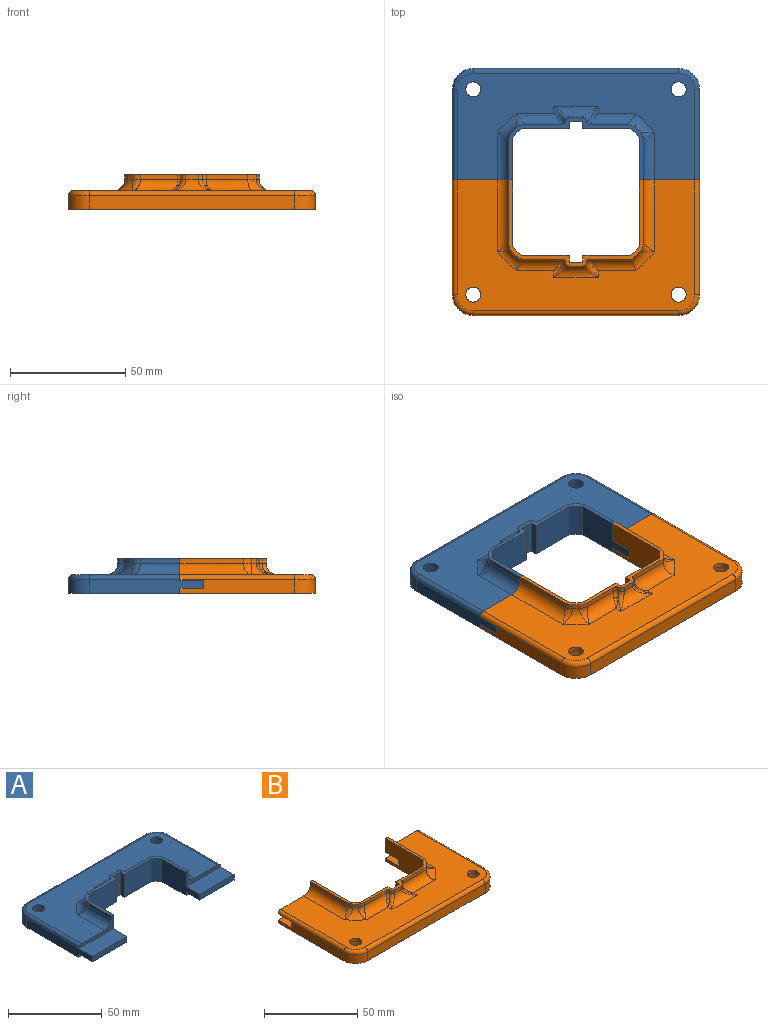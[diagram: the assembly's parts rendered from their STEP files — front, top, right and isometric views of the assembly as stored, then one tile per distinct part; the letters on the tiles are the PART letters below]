
ASSEMBLY  parts=2 mates=1
PART A: 73 faces, bbox 108.5x59.2x16.6 mm
  f0: plane 49.43x6mm, normal (1,0,0), area 272.4mm2, adj f1,f66,f67,f68,f69,f70,f71,f72
  f1: plane 26x10.2mm, normal (0,0,-1), area 265.2mm2, adj f0,f2,f66,f72
  f2: plane 28.6x15mm, normal (-1,0,0), area 313mm2, adj f1,f3,f65,f66,f67,f68,f71,f72
  f3: cylinder r=36.25mm len=15mm, axis (0,0,-1), area 82.4mm2, adj f2,f4,f65,f71
  f4: plane 20.62x15mm, normal (0,-1,0), area 309.3mm2, adj f3,f5,f65,f71
  f5: plane 15x3mm, normal (-1,0,0), area 45mm2, adj f4,f6,f65,f71
  f6: plane 15x6mm, normal (0,-1,0), area 90mm2, adj f5,f7,f65,f71
  f7: plane 15x3mm, normal (1,0,0), area 45mm2, adj f6,f8,f65,f71
  f8: plane 20.62x15mm, normal (0,-1,0), area 309.3mm2, adj f7,f9,f65,f71
  f9: cylinder r=36.25mm len=15mm, axis (0,0,-1), area 82.4mm2, adj f8,f10,f65,f71
  f10: plane 28.6x15mm, normal (1,0,0), area 313mm2, adj f9,f11,f61,f62,f63,f64,f65,f71
  f11: plane 26x10.2mm, normal (0,0,-1), area 265.2mm2, adj f10,f12,f61,f64
  f12: plane 49.43x6mm, normal (-1,0,0), area 272.4mm2, adj f11,f13,f60,f61,f62,f63,f64,f71
  f13: cylinder r=9.05mm len=9.05mm, axis (0,0,-1), area 85.3mm2, adj f12,f14,f59,f71
  f14: plane 88.9x6mm, normal (0,1,0), area 533.4mm2, adj f13,f15,f70,f71
  f15: cylinder r=2mm len=88.9mm, axis (1,0,0), area 279.3mm2, adj f14,f16,f17,f59
  f16: torus R=7.05mm, axis (0,0,1), area 41.1mm2, adj f15,f17,f69,f70
  f17: plane 103x46.28mm, normal (0,0,1), area 2712.4mm2, adj f15,f16,f18,f44,f45,f47,f48,f49
  f18: cylinder r=5mm len=20.73mm, axis (0,1,0), area 148.6mm2, adj f17,f19,f43,f68
  f19: bspline ~6.34x5.9mm, area 11.8mm2, adj f18,f20,f44
  f20: cylinder r=5mm len=3.4mm, axis (0,0,-1), area 7.5mm2, adj f19,f21,f43,f65
  f21: cylinder r=37.85mm len=2.04mm, axis (0,0,-1), area 5.8mm2, adj f20,f22,f44,f65
  f22: cylinder r=5mm len=3.4mm, axis (0,0,-1), area 7.5mm2, adj f21,f23,f42,f65
  f23: plane 16.26x2mm, normal (0,1,0), area 32.5mm2, adj f22,f24,f45,f65
  f24: cylinder r=1.5mm len=2mm, axis (0,0,-1), area 4.3mm2, adj f23,f25,f28,f65
  f25: bspline ~4.79x2.55mm, area 6.2mm2, adj f24,f26,f27,f45
  f26: bspline ~2.94x2.94mm, area 2.5mm2, adj f25,f45,f47
  f27: bspline ~7x7mm, area 13.9mm2, adj f25,f28,f47,f48
  f28: cylinder r=2mm len=2mm, axis (0,0,-1), area 5.7mm2, adj f24,f27,f29,f65
  f29: plane 5.2x2mm, normal (0,1,0), area 10.4mm2, adj f28,f30,f48,f65
  f30: cylinder r=2mm len=2mm, axis (0,0,-1), area 5.7mm2, adj f29,f31,f41,f65
  f31: cylinder r=1.5mm len=2mm, axis (0,0,-1), area 4.3mm2, adj f30,f32,f34,f65
  f32: bspline ~4.4x2.38mm, area 6.2mm2, adj f31,f33,f41,f50
  f33: bspline ~4.49x4.49mm, area 4mm2, adj f32,f49,f50
  f34: plane 16.26x2mm, normal (0,1,0), area 32.5mm2, adj f31,f35,f50,f65
  f35: cylinder r=5mm len=3.4mm, axis (0,0,-1), area 7.5mm2, adj f34,f36,f40,f65
  f36: cylinder r=37.85mm len=2.04mm, axis (0,0,-1), area 5.8mm2, adj f35,f37,f51,f65
  f37: cylinder r=5mm len=3.4mm, axis (0,0,-1), area 7.5mm2, adj f36,f38,f39,f65
  f38: plane 17.11x2mm, normal (-1,0,0), area 34.2mm2, adj f37,f52,f63,f65
  f39: bspline ~6.34x5.9mm, area 11.8mm2, adj f37,f51,f52
  f40: bspline ~6.34x5.9mm, area 11.8mm2, adj f35,f50,f51
  f41: bspline ~7x7mm, area 13.9mm2, adj f30,f32,f48,f49
  f42: bspline ~6.34x5.9mm, area 11.8mm2, adj f22,f44,f45
  f43: plane 17.11x2mm, normal (1,0,0), area 34.2mm2, adj f18,f20,f65,f68
  f44: torus R=42.85mm, axis (0,0,1), area 54.6mm2, adj f17,f19,f21,f42
  f45: cylinder r=5mm len=19.89mm, axis (-1,0,0), area 130.7mm2, adj f17,f23,f25,f26,f42,f46
  f46: bspline ~2.91x2.91mm, area 0.6mm2, adj f45,f47
  f47: cylinder r=5mm len=6mm, axis (0,1,0), area 7.7mm2, adj f17,f26,f27,f46
  f48: cylinder r=5mm len=19.2mm, axis (-1,0,0), area 95.8mm2, adj f17,f27,f29,f41
  f49: cylinder r=5mm len=6mm, axis (0,1,0), area 7.7mm2, adj f17,f33,f41
  f50: cylinder r=5mm len=19.89mm, axis (-1,0,0), area 130.7mm2, adj f17,f32,f33,f34,f40
  f51: torus R=42.85mm, axis (0,0,1), area 54.6mm2, adj f17,f36,f39,f40
  f52: cylinder r=5mm len=20.73mm, axis (0,-1,0), area 148.6mm2, adj f17,f38,f39,f63
  f53: cylinder r=3.25mm len=6.5mm, axis (0,0,-1), area 40.8mm2, adj f17,f54
  f54: plane 13x13mm, normal (0,0,-1), area 99.5mm2, adj f53,f55
  f55: cylinder r=6.5mm len=13mm, axis (0,0,-1), area 245mm2, adj f54,f71
  f56: cylinder r=3.25mm len=6.5mm, axis (0,0,-1), area 40.8mm2, adj f17,f57
  f57: plane 13x13mm, normal (0,0,-1), area 99.5mm2, adj f56,f58
  f58: cylinder r=6.5mm len=13mm, axis (0,0,-1), area 245mm2, adj f57,f71
  f59: torus R=7.05mm, axis (0,0,1), area 41.1mm2, adj f13,f15,f17,f60
  f60: cylinder r=2mm len=39.23mm, axis (0,1,0), area 123.3mm2, adj f12,f17,f59,f63
  f61: plane 26x3.62mm, normal (0,-1,0), area 94.2mm2, adj f10,f11,f12,f62
  f62: plane 26x10.2mm, normal (0,0,1), area 265.2mm2, adj f10,f12,f61,f63
  f63: plane 26x9.25mm, normal (0,-1,0), area 74.2mm2, adj f10,f12,f17,f38,f52,f60,f62,f65
  f64: plane 26x2.13mm, normal (0,-1,0), area 55.3mm2, adj f10,f11,f12,f71
  f65: plane 58.2x26.88mm, normal (0,0,1), area 163.3mm2, adj f2,f3,f4,f5,f6,f7,f8,f9
  f66: plane 26x3.62mm, normal (0,-1,0), area 94.2mm2, adj f0,f1,f2,f67
  f67: plane 26x10.2mm, normal (0,0,1), area 265.2mm2, adj f0,f2,f66,f68
  f68: plane 26x9.25mm, normal (0,-1,0), area 74.2mm2, adj f0,f2,f17,f18,f43,f65,f67,f69
  f69: cylinder r=2mm len=39.23mm, axis (0,-1,0), area 123.3mm2, adj f0,f16,f17,f68
  f70: cylinder r=9.05mm len=9.05mm, axis (0,0,-1), area 85.3mm2, adj f0,f14,f16,f71
  f71: plane 107x48.28mm, normal (0,0,-1), area 3636.4mm2, adj f0,f2,f3,f4,f5,f6,f7,f8
  f72: plane 26x2.13mm, normal (0,-1,0), area 55.3mm2, adj f0,f1,f2,f71
PART B: 70 faces, bbox 108.5x59.5x16.6 mm
  f0: plane 49.67x6mm, normal (1,0,0), area 255.9mm2, adj f6,f8,f39,f59,f62,f63
  f1: cylinder r=6.5mm len=13mm, axis (0,0,-1), area 245mm2, adj f8,f12
  f2: cylinder r=6.5mm len=13mm, axis (0,0,-1), area 245mm2, adj f8,f10
  f3: plane 49.67x6mm, normal (-1,0,0), area 255.9mm2, adj f4,f8,f40,f54,f57,f58
  f4: cylinder r=9.05mm len=9.05mm, axis (0,0,-1), area 85.3mm2, adj f3,f5,f8,f42
  f5: plane 88.9x6mm, normal (0,-1,0), area 533.4mm2, adj f4,f6,f8,f43
  f6: cylinder r=9.05mm len=9.05mm, axis (0,0,-1), area 85.3mm2, adj f0,f5,f8,f41
  f7: plane 103x56.72mm, normal (0,0,1), area 3075.6mm2, adj f9,f11,f30,f31,f32,f33,f34,f35
  f8: plane 107x58.72mm, normal (0,0,-1), area 4179mm2, adj f0,f1,f2,f3,f4,f5,f6,f20
  f9: cylinder r=3.25mm len=6.5mm, axis (0,0,-1), area 40.8mm2, adj f7,f10
  f10: plane 13x13mm, normal (0,0,-1), area 99.5mm2, adj f2,f9
  f11: cylinder r=3.25mm len=6.5mm, axis (0,0,-1), area 40.8mm2, adj f7,f12
  f12: plane 13x13mm, normal (0,0,-1), area 99.5mm2, adj f1,f11
  f13: plane 18.14x2mm, normal (0,-1,0), area 36.3mm2, adj f14,f29,f36,f69
  f14: cylinder r=37.85mm len=3.56mm, axis (0,0,-1), area 9.8mm2, adj f13,f29,f37,f53
  f15: plane 27.54x2mm, normal (1,0,0), area 55.1mm2, adj f29,f38,f53,f60
  f16: plane 27.54x2mm, normal (-1,0,0), area 55.1mm2, adj f29,f34,f51,f56
  f17: cylinder r=37.85mm len=2.04mm, axis (0,0,-1), area 5.8mm2, adj f29,f32,f49,f51
  f18: plane 16.26x2mm, normal (0,-1,0), area 32.5mm2, adj f29,f30,f49,f66
  f19: plane 5.2x2mm, normal (0,-1,0), area 10.4mm2, adj f29,f33,f45,f47
  f20: plane 15x6mm, normal (0,1,0), area 90mm2, adj f8,f21,f28,f29
  f21: plane 15x3mm, normal (1,0,0), area 45mm2, adj f8,f20,f22,f29
  f22: plane 20.62x15mm, normal (0,1,0), area 309.3mm2, adj f8,f21,f23,f29
  f23: cylinder r=36.25mm len=15mm, axis (0,0,-1), area 82.4mm2, adj f8,f22,f24,f29
  f24: plane 28.84x15mm, normal (1,0,0), area 390.5mm2, adj f8,f23,f29,f54,f55,f56,f57,f58
  f25: plane 28.84x15mm, normal (-1,0,0), area 390.5mm2, adj f8,f26,f29,f59,f60,f61,f62,f63
  f26: cylinder r=36.25mm len=15mm, axis (0,0,-1), area 82.4mm2, adj f8,f25,f27,f29
  f27: plane 20.62x15mm, normal (0,1,0), area 309.3mm2, adj f8,f26,f28,f29
  f28: plane 15x3mm, normal (-1,0,0), area 45mm2, adj f8,f20,f27,f29
  f29: plane 58.2x37.32mm, normal (0,0,1), area 197.1mm2, adj f13,f14,f15,f16,f17,f18,f19,f20
  f30: cylinder r=5mm len=19.89mm, axis (1,0,0), area 130.7mm2, adj f7,f18,f48,f64,f65
  f31: cylinder r=5mm len=6mm, axis (0,1,0), area 7.7mm2, adj f7,f44,f64
  f32: torus R=42.85mm, axis (0,0,1), area 54.6mm2, adj f7,f17,f48,f50
  f33: cylinder r=5mm len=19.62mm, axis (1,0,0), area 95.8mm2, adj f7,f19,f44,f46
  f34: cylinder r=5mm len=31.17mm, axis (0,-1,0), area 230.6mm2, adj f7,f16,f50,f56
  f35: cylinder r=5mm len=6mm, axis (0,1,0), area 7.7mm2, adj f7,f46,f67
  f36: cylinder r=5mm len=19.89mm, axis (1,0,0), area 138.1mm2, adj f7,f13,f37,f67,f68
  f37: torus R=42.85mm, axis (0,0,1), area 62.7mm2, adj f7,f14,f36,f52
  f38: cylinder r=5mm len=31.17mm, axis (0,1,0), area 230.6mm2, adj f7,f15,f52,f60
  f39: cylinder r=2mm len=49.67mm, axis (0,-1,0), area 156mm2, adj f0,f7,f41,f60,f61
  f40: cylinder r=2mm len=49.67mm, axis (0,1,0), area 156mm2, adj f3,f7,f42,f55,f56
  f41: torus R=7.05mm, axis (0,0,1), area 41.1mm2, adj f6,f7,f39,f43
  f42: torus R=7.05mm, axis (0,0,1), area 41.1mm2, adj f4,f7,f40,f43
  f43: cylinder r=2mm len=88.9mm, axis (-1,0,0), area 279.3mm2, adj f5,f7,f41,f42
  f44: bspline ~7x7mm, area 13.9mm2, adj f31,f33,f45,f65
  f45: cylinder r=2mm len=2mm, axis (0,0,1), area 5.7mm2, adj f19,f29,f44,f66
  f46: bspline ~7x7mm, area 6.6mm2, adj f33,f35,f47,f68
  f47: cylinder r=2mm len=2mm, axis (0,0,-1), area 5.7mm2, adj f19,f29,f46,f69
  f48: bspline ~6.34x5.9mm, area 11.8mm2, adj f30,f32,f49
  f49: cylinder r=5mm len=3.4mm, axis (0,0,-1), area 7.5mm2, adj f17,f18,f29,f48
  f50: bspline ~6.34x5.9mm, area 11.8mm2, adj f32,f34,f51
  f51: cylinder r=5mm len=3.4mm, axis (0,0,-1), area 7.5mm2, adj f16,f17,f29,f50
  f52: bspline ~6.34x5.9mm, area 11.8mm2, adj f37,f38,f53
  f53: cylinder r=5mm len=3.4mm, axis (0,0,-1), area 7.5mm2, adj f14,f15,f29,f52
  f54: plane 26x10.2mm, normal (0,0,1), area 265.2mm2, adj f3,f24,f57,f58
  f55: plane 26x10.2mm, normal (0,0,-1), area 265.2mm2, adj f24,f40,f56,f57
  f56: plane 26x9mm, normal (0,1,0), area 67.7mm2, adj f7,f16,f24,f29,f34,f40,f55
  f57: plane 26x4.12mm, normal (0,1,0), area 107.2mm2, adj f3,f24,f54,f55
  f58: plane 26x1.88mm, normal (0,1,0), area 48.8mm2, adj f3,f8,f24,f54
  f59: plane 26x1.88mm, normal (0,1,0), area 48.8mm2, adj f0,f8,f25,f63
  f60: plane 26x9mm, normal (0,1,0), area 67.7mm2, adj f7,f15,f25,f29,f38,f39,f61
  f61: plane 26x10.2mm, normal (0,0,-1), area 265.2mm2, adj f25,f39,f60,f62
  f62: plane 26x4.12mm, normal (0,1,0), area 107.2mm2, adj f0,f25,f61,f63
  f63: plane 26x10.2mm, normal (0,0,1), area 265.2mm2, adj f0,f25,f59,f62
  f64: bspline ~4.49x4.49mm, area 4mm2, adj f30,f31,f65
  f65: bspline ~4.79x2.55mm, area 6.2mm2, adj f30,f44,f64,f66
  f66: cylinder r=1.5mm len=2mm, axis (0,0,1), area 4.3mm2, adj f18,f29,f45,f65
  f67: bspline ~4.49x4.49mm, area 4mm2, adj f35,f36,f68
  f68: bspline ~4.4x2.38mm, area 6.2mm2, adj f36,f46,f67,f69
  f69: cylinder r=1.5mm len=2mm, axis (0,0,-1), area 4.3mm2, adj f13,f29,f47,f68
PLACE A t=(-3.71,-40.15,9.56)mm
PLACE B t=(-3.71,-40.15,9.56)mm
MATE fastened B.f56 <-> A.f63  axis (0,1,0) through (-31.21,-34.93,24.56)mm
